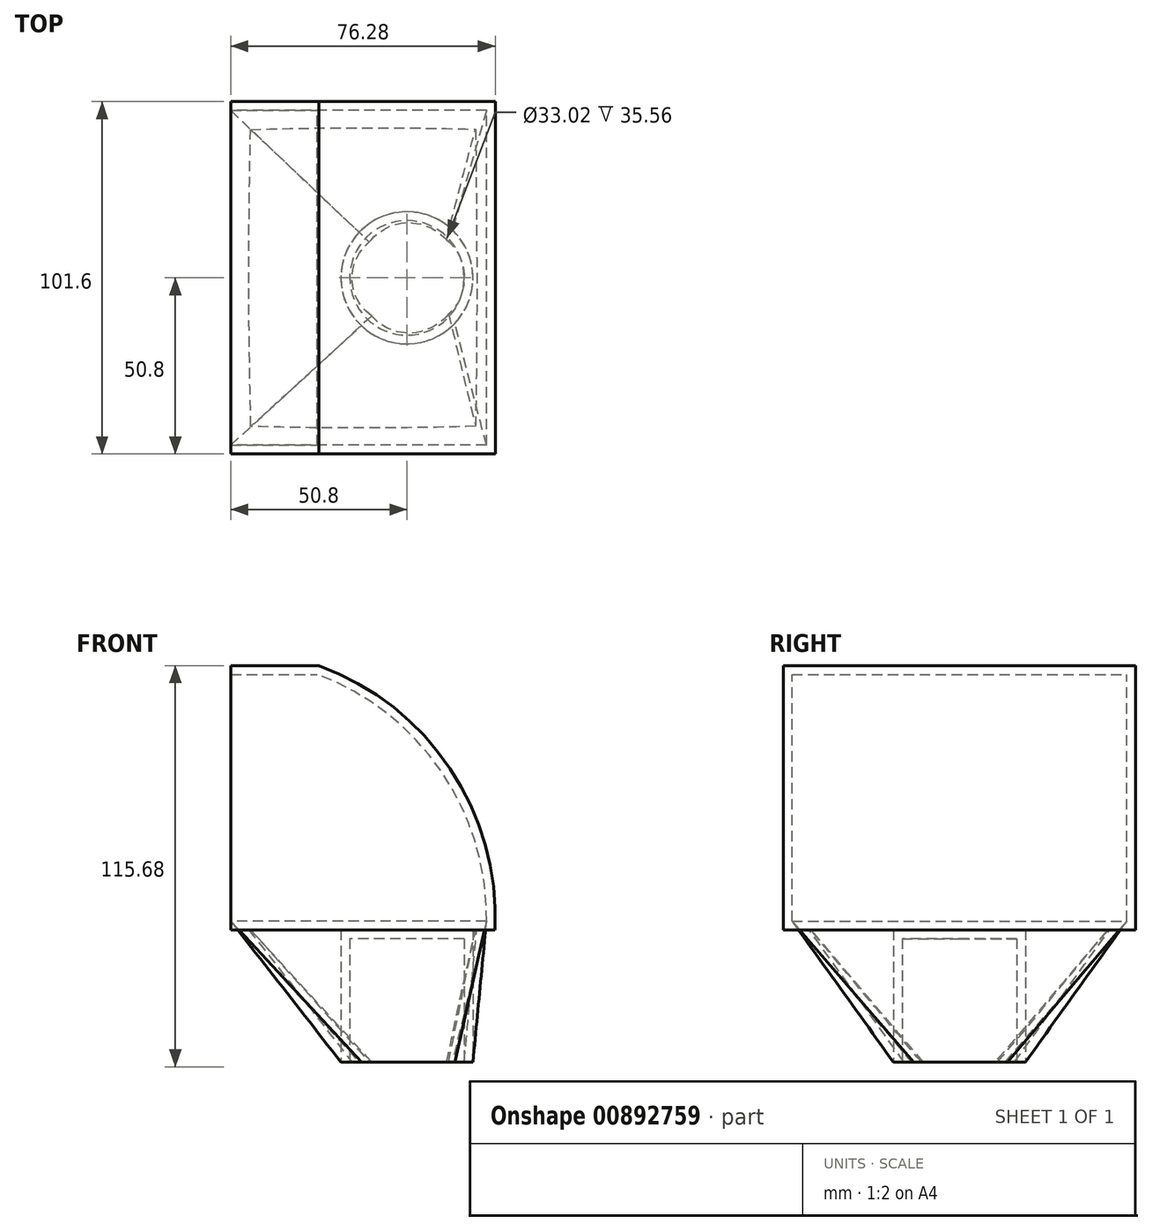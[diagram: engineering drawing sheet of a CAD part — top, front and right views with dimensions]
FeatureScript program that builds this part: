
annotation { "Feature Type Name" : "Feature", "Feature Type Description" : "" }
export const myFeature = defineFeature(function(context is Context, id is Id, definition is map)
    precondition{}
    {
        {
            var Q0;
            Q0=qCreatedBy(makeId("Front.planeOp"),FACE);
            var sketch = newSketch(context, id + "F0", { "sketchPlane" : qUnion([Q0])});
            skLineSegment(sketch, "E0", {"start": v(0, 0) * mm, "end": v(-25.4, 0) * mm});
            skLineSegment(sketch, "E1", {"start": v(-25.4, 0) * mm, "end": v(-25.4, 76.2) * mm});
            skLineSegment(sketch, "E2", {"start": v(-25.4, 76.2) * mm, "end": v(0, 76.2) * mm});
            skLineSegment(sketch, "E3", {"start": v(0, 76.2) * mm, "end": v(0, 0) * mm});
            skLineSegment(sketch, "E4", {"start": v(0, 0) * mm, "end": v(50.8, 0) * mm});
            skArc(sketch, "E5", {"start": v(50.8, 0) * mm, "mid": v(37.9, 46.43) * mm, "end": v(0, 76.2) * mm});
            skSolve(sketch);
        }
        {
            var Q0;
            Q0 = qSketchRegion(id + "F0", true);
            extrude(context, id + "F1", {"entities" : qUnion([Q0]), "depth" : 101.6 * mm, "offsetDistance" : 25.4 * mm});
        }
        {
            var Q0;
            Q0=qCreatedBy(makeId("Top.planeOp"),FACE);
            cPlane(context, id + "F2", {"entities" : qUnion([Q0]), "cplaneType" : CPlaneType.OFFSET, "offset" : 38.1 * mm, "oppositeDirection" : true, "width" : 152.4 * mm, "height" : 152.4 * mm});
        }
        {
            var Q0;
            Q0=qCreatedBy(id+"F2.planeOp",FACE);
            var sketch = newSketch(context, id + "F3", { "sketchPlane" : qUnion([Q0])});
            skLineSegment(sketch, "E6", {"start": v(0, 0) * mm, "end": v(25.4, 0) * mm});
            skLineSegment(sketch, "E7", {"start": v(25.4, 0) * mm, "end": v(25.4, -50.8) * mm});
            skCircle(sketch, "E8", {"center": v(25.4, -50.8) * mm, "radius": 19.05 * mm});
            skSolve(sketch);
        }
        {
            var Q0;
            Q0=makeQuery(id+"F3.imprint","IMPRINT",FACE,{"disambiguationData":[TD([[makeQuery(id+"F3.imprint","IMPRINT",EDGE,{"derivedFrom":sQuery(id+"F3.wireOp",EDGE,"E8")}),1.0]])]});
            extrude(context, id + "F4", {"entities" : qUnion([Q0]), "depth" : 38.1 * mm, "offsetDistance" : 25.4 * mm});
        }
        {
            var Q0;
            Q0=makeQuery(id+"F1.opExtrude","SWEPT_FACE",FACE,{"disambiguationData":[OSD([sQuery(id+"F0.wireOp",EDGE,"E1")])]});
            shell(context, id + "F5", {"entities" : qUnion([Q0]), "thickness" : 2.54 * mm});
        }
        {
            var Q0;
            Q0=makeQuery(id+"F5.opShell","OFFSET_FACE",FACE,{"disambiguationData":[OSD([sQuery(id+"F0.wireOp",EDGE,"E0"),sQuery(id+"F0.wireOp",EDGE,"E4")])]});
            var Q1;
            Q1=makeQuery(id+"F4.opExtrude","CAP_FACE",FACE,{"disambiguationData":[OSD([sQuery(id+"F3.wireOp",EDGE,"E8")])],"isStart":true});
            loft(context, id + "F6", {"sheetProfilesArray" : [{ "sheetProfileEntities" : qUnion([Q0]) }, { "sheetProfileEntities" : qUnion([Q1]) }]});
        }
        {
            var Q0;
            Q0=makeQuery(id+"F4.opExtrude","CAP_FACE",FACE,{"disambiguationData":[OSD([sQuery(id+"F3.wireOp",EDGE,"E8")])],"isStart":true});
            var Q1;
            Q1=makeQuery(id+"F6.opLoft","CAP_FACE",FACE,{"disambiguationData":[OSD([sQuery(id+"F3.wireOp",EDGE,"E8")])],"isStart":true});
            shell(context, id + "F7", {"entities" : qUnion([Q0, Q1]), "thickness" : 2.54 * mm});
        }
    });
